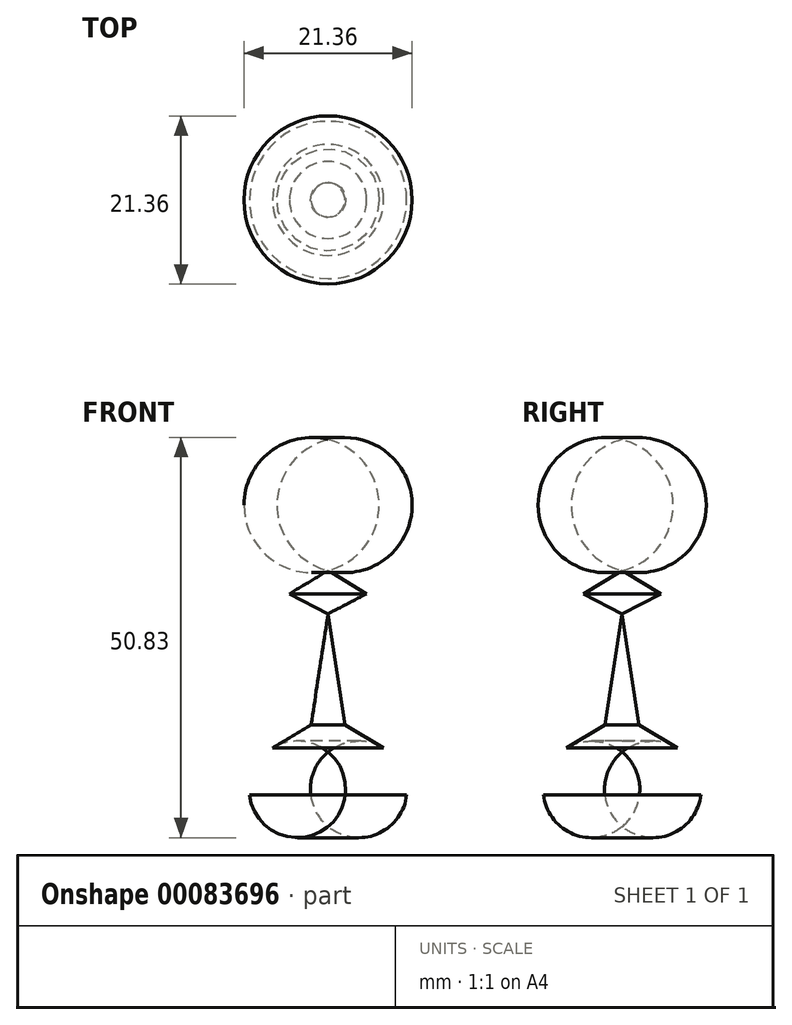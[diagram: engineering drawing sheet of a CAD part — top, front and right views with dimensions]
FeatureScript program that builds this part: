
annotation { "Feature Type Name" : "Feature", "Feature Type Description" : "" }
export const myFeature = defineFeature(function(context is Context, id is Id, definition is map)
    precondition{}
    {
        {
            var Q0;
            Q0=qCreatedBy(makeId("Front.planeOp"),FACE);
            var sketch = newSketch(context, id + "F0", { "sketchPlane" : qUnion([Q0])});
            skLineSegment(sketch, "E0", {"start": v(0, 0) * mm, "end": v(0, 45.15) * mm});
            skArc(sketch, "E1", {"start": v(0, 28.5) * mm, "mid": v(6.49, 36.82) * mm, "end": v(0, 45.15) * mm});
            skSolve(sketch);
        }
        {
            var Q0;
            Q0=qCreatedBy(makeId("Front.planeOp"),FACE);
            var sketch = newSketch(context, id + "F1", { "sketchPlane" : qUnion([Q0])});
            skLineSegment(sketch, "E2", {"start": v(0, 28.5) * mm, "end": v(4.9, 25.56) * mm});
            skLineSegment(sketch, "E3", {"start": v(4.9, 25.56) * mm, "end": v(0, 23.01) * mm});
            skLineSegment(sketch, "E4", {"start": v(0, 23.01) * mm, "end": v(2.15, 8.91) * mm});
            skLineSegment(sketch, "E5", {"start": v(2.15, 8.91) * mm, "end": v(7.05, 5.97) * mm});
            skArc(sketch, "E6", {"start": v(9.99, 0) * mm, "mid": v(9.4, 3.42) * mm, "end": v(7.05, 5.97) * mm});
            skLineSegment(sketch, "E7", {"start": v(9.99, 0) * mm, "end": v(0, 0) * mm});
            skLineSegment(sketch, "E8", {"start": v(0, 0) * mm, "end": v(0, 44.75) * mm});
            skSolve(sketch);
        }
        {
            var Q0;
            {var subQ0=sQuery(id+"F0.wireOp",EDGE,"E1");Q0=makeQuery(id+"F0.imprint","IMPRINT",FACE,{"disambiguationData":[TD([[makeQuery(id+"F0.imprint","IMPRINT",EDGE,{"derivedFrom":subQ0}),1.0]])]});}
            var Q1;
            {var subQ0=sQuery(id+"F1.wireOp",EDGE,"E2");Q1=makeQuery(id+"F1.imprint","IMPRINT",FACE,{"disambiguationData":[TD([[makeQuery(id+"F1.imprint","IMPRINT",EDGE,{"derivedFrom":subQ0}),-1.0]])]});}
            var Q2;
            {var subQ1=sQuery(id+"F1.wireOp",EDGE,"E4");Q2=makeQuery(id+"F1.imprint","IMPRINT",FACE,{"disambiguationData":[TD([[makeQuery(id+"F1.imprint","IMPRINT",EDGE,{"derivedFrom":subQ1}),-1.0]])]});}
            var Q3;
            Q3=sQuery(id+"F1.wireOp",EDGE,"E8");
            revolve(context, id + "F2", {"entities" : qUnion([Q0, Q1, Q2]), "axis" : qUnion([Q3]), "revolveType" : RevolveType.FULL});
        }
    });
